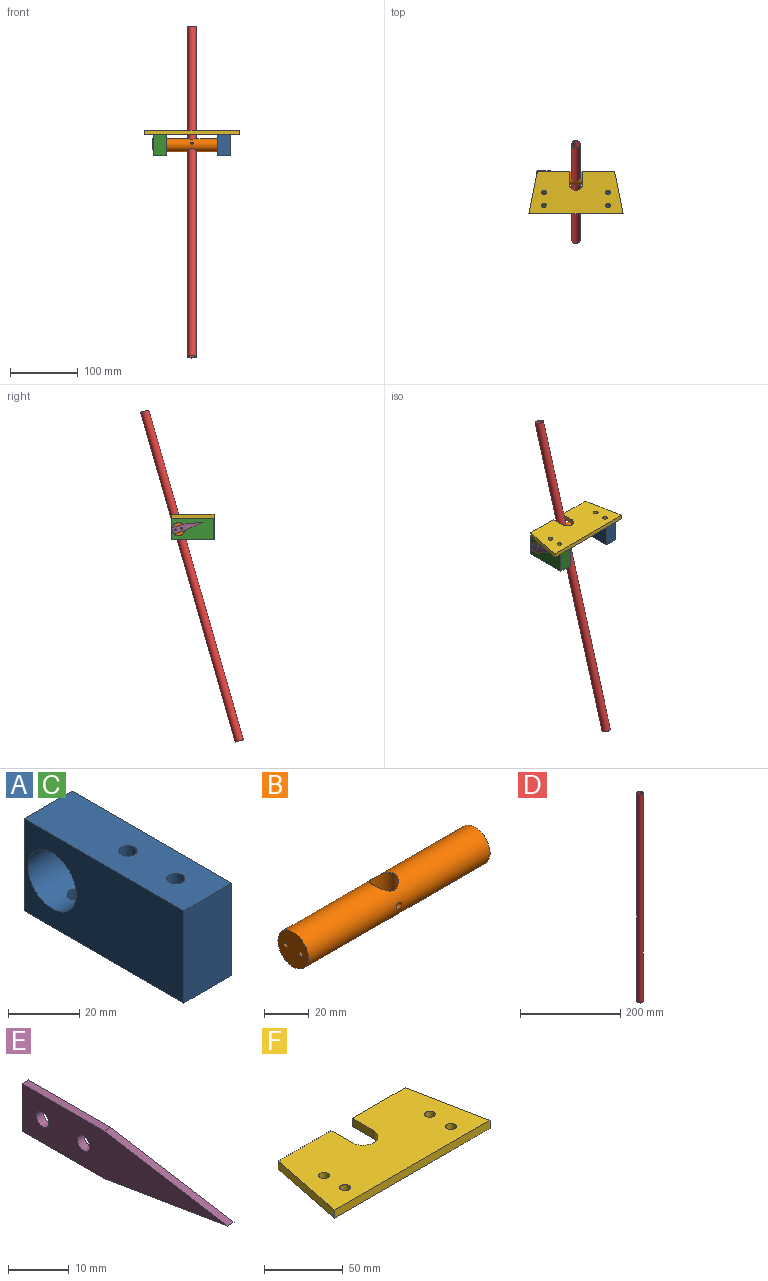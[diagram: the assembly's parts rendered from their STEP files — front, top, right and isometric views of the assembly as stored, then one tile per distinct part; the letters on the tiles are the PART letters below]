
ASSEMBLY  parts=6 mates=4
PART A: 12 faces, bbox 19.1x63.5x31.8 mm
  f0: cylinder r=9.62mm len=19.24mm, axis (-1,0,0), area 1130.9mm2, adj f5,f6,f7
  f1: plane 63.5x19.05mm, normal (0,0,1), area 1168.7mm2, adj f2,f4,f5,f6,f8,f10
  f2: plane 31.75x19.05mm, normal (0,-1,0), area 604.8mm2, adj f1,f3,f5,f6
  f3: plane 63.5x19.05mm, normal (0,0,-1), area 1189.2mm2, adj f2,f4,f5,f6,f7
  f4: plane 31.75x19.05mm, normal (0,1,0), area 604.8mm2, adj f1,f3,f5,f6
  f5: plane 63.5x31.75mm, normal (-1,0,0), area 1725.4mm2, adj f0,f1,f2,f3,f4
  f6: plane 63.5x31.75mm, normal (1,0,0), area 1725.4mm2, adj f0,f1,f2,f3,f4
  f7: cylinder r=2.55mm len=6.6mm, axis (0,0,-1), area 103.1mm2, adj f0,f3
  f8: cylinder r=2.55mm len=16.51mm, axis (0,0,1), area 264.8mm2, adj f1,f9
  f9: cone r=0mm half-angle=59deg, axis (0,0,1), area 23.9mm2, adj f8
  f10: cylinder r=2.55mm len=16.51mm, axis (0,0,1), area 264.8mm2, adj f1,f11
  f11: cone r=0mm half-angle=59deg, axis (0,0,1), area 23.9mm2, adj f10
PART B: 10 faces, bbox 114.3x19.1x19.1 mm
  f0: cylinder r=9.53mm len=114.3mm, axis (-1,0,0), area 6555.1mm2, adj f1,f2,f3,f5
  f1: cylinder r=6.41mm len=19.05mm, axis (0,0,1), area 660.9mm2, adj f0,f4,f5
  f2: plane 19.05x19.05mm, normal (1,0,0), area 285mm2, adj f0
  f3: plane 19.05x19.05mm, normal (-1,0,0), area 277mm2, adj f0,f6,f8
  f4: cone r=0mm half-angle=59deg, axis (0,-1,0), area 1.3mm2, adj f1
  f5: cylinder r=1.73mm len=3.45mm, axis (0,-1,0), area 34.2mm2, adj f0,f1
  f6: cylinder r=1.13mm len=14.61mm, axis (-1,0,0), area 103.7mm2, adj f3,f7
  f7: cone r=0mm half-angle=59deg, axis (-1,0,0), area 4.7mm2, adj f6
  f8: cylinder r=1.13mm len=14.61mm, axis (-1,0,0), area 103.7mm2, adj f3,f9
  f9: cone r=0mm half-angle=59deg, axis (-1,0,0), area 4.7mm2, adj f8
PART C: same geometry as A
PART D: 4 faces, bbox 12.7x12.7x508 mm
  f0: cylinder r=5.56mm len=508mm, axis (0,0,-1), area 17734.8mm2, adj f2,f3
  f1: cylinder r=6.35mm len=508mm, axis (0,0,-1), area 20268.3mm2, adj f2,f3
  f2: plane 12.7x12.7mm, normal (0,0,1), area 29.7mm2, adj f0,f1
  f3: plane 12.7x12.7mm, normal (0,0,-1), area 29.7mm2, adj f0,f1
PART E: 9 faces, bbox 1.6x47.6x9.5 mm
  f0: plane 9.53x1.59mm, normal (0,1,0), area 15.1mm2, adj f1,f4,f5,f6
  f1: plane 19.05x1.59mm, normal (0,0,1), area 30.2mm2, adj f0,f2,f5,f6
  f2: plane 28.58x4.76mm, normal (0,-0.16,0.99), area 46mm2, adj f1,f3,f5,f6
  f3: plane 28.58x4.76mm, normal (0,-0.16,-0.99), area 46mm2, adj f2,f4,f5,f6
  f4: plane 19.05x1.59mm, normal (0,0,-1), area 30.2mm2, adj f0,f3,f5,f6
  f5: plane 47.63x9.53mm, normal (1,0,0), area 303.9mm2, adj f0,f1,f2,f3,f4,f7,f8
  f6: plane 47.63x9.53mm, normal (-1,0,0), area 303.9mm2, adj f0,f1,f2,f3,f4,f7,f8
  f7: cylinder r=1.47mm len=2.95mm, axis (-1,0,0), area 14.7mm2, adj f5,f6
  f8: cylinder r=1.47mm len=2.95mm, axis (-1,0,0), area 14.7mm2, adj f5,f6
PART F: 14 faces, bbox 139.7x63.5x6.4 mm
  f0: plane 47.63x6.35mm, normal (0,1,0), area 302.4mm2, adj f1,f5,f6,f12
  f1: plane 139.7x63.5mm, normal (0,0,1), area 7415.7mm2, adj f0,f2,f3,f4,f5,f7,f8,f9
  f2: plane 47.63x6.35mm, normal (0,1,0), area 302.4mm2, adj f1,f3,f6,f13
  f3: plane 63.5x12.7mm, normal (-0.98,0.2,0), area 411.2mm2, adj f1,f2,f4,f6
  f4: plane 139.7x6.35mm, normal (0,-1,0), area 887.1mm2, adj f1,f3,f5,f6
  f5: plane 63.5x12.7mm, normal (0.98,0.2,0), area 411.2mm2, adj f0,f1,f4,f6
  f6: plane 139.7x63.5mm, normal (0,0,-1), area 7415.7mm2, adj f0,f2,f3,f4,f5,f7,f8,f9
  f7: cylinder r=3.38mm len=6.76mm, axis (0,0,1), area 134.8mm2, adj f1,f6
  f8: cylinder r=3.38mm len=6.76mm, axis (0,0,1), area 134.8mm2, adj f1,f6
  f9: cylinder r=3.38mm len=6.76mm, axis (0,0,1), area 134.8mm2, adj f1,f6
  f10: cylinder r=3.38mm len=6.76mm, axis (0,0,1), area 134.8mm2, adj f1,f6
  f11: cylinder r=9.53mm len=19.05mm, axis (0,0,1), area 190mm2, adj f1,f6,f12,f13
  f12: plane 19.05x6.35mm, normal (-1,0,0), area 121mm2, adj f0,f1,f6,f11
  f13: plane 19.05x6.35mm, normal (1,0,0), area 121mm2, adj f1,f2,f6,f11
PLACE A t=(95.25,0,0)mm
PLACE B rot(axis=(-1,0,0),16deg) t=(0,0.16,0)mm
PLACE C t=(0,0.16,0)mm
PLACE D rot(axis=(-1,0,0),16deg) t=(0,36.26,125.9)mm
PLACE E rot(axis=(-1,0,0),16deg) t=(-58.74,-0.03,0.06)mm
PLACE F at identity fixed
MATE fastened E.f5 <-> B.f3  axis (1,0,0) through (-57.15,-8.23,2.41)mm
MATE fastened C.f1 <-> F.f6  axis (0,0,1) through (-47.63,11.27,15.88)mm
MATE revolute B.f0 <-> C.f0  axis (-1,0,0) through (0,0.16,0)mm
MATE slider D.f0 <-> B.f1  axis (0,-0.28,-0.96) through (0,-89.76,-313.59)mm
